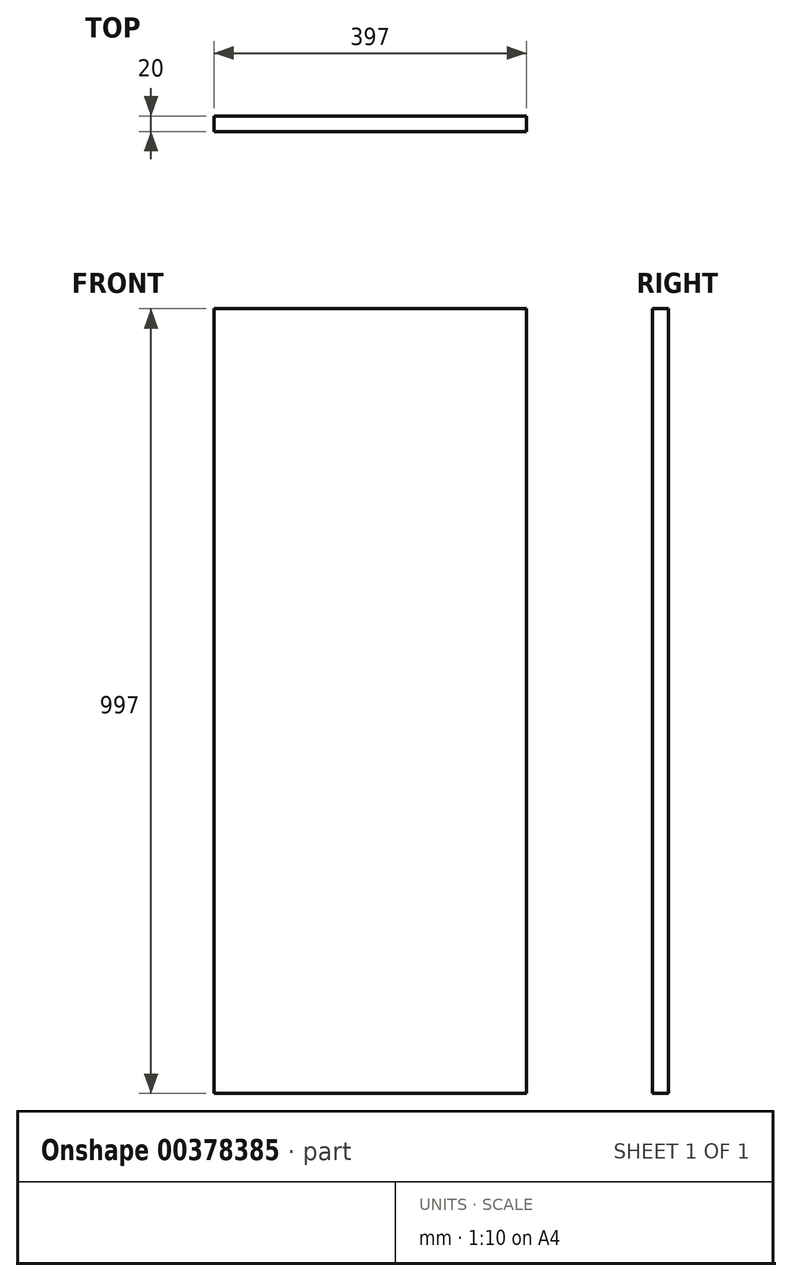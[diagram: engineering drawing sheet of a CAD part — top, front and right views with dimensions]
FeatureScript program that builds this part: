
annotation { "Feature Type Name" : "Feature", "Feature Type Description" : "" }
export const myFeature = defineFeature(function(context is Context, id is Id, definition is map)
    precondition{}
    {
        {
            var Q0;
            Q0=qCreatedBy(makeId("Front.planeOp"),FACE);
            var sketch = newSketch(context, id + "F0", { "sketchPlane" : qUnion([Q0])});
            skLineSegment(sketch, "E0.bottom", {"start": v(198.5, 498.5) * mm, "end": v(-198.5, 498.5) * mm});
            skLineSegment(sketch, "E0.top", {"start": v(198.5, -498.5) * mm, "end": v(-198.5, -498.5) * mm});
            skLineSegment(sketch, "E0.left", {"start": v(198.5, 498.5) * mm, "end": v(198.5, -498.5) * mm});
            skLineSegment(sketch, "E0.right", {"start": v(-198.5, 498.5) * mm, "end": v(-198.5, -498.5) * mm});
            skPoint(sketch, "E0.middle", {"position": v(0, 0) * mm});
            skSolve(sketch);
        }
        {
            var Q0;
            Q0=qSketchRegion(id+"F0",true);
            extrude(context, id + "F1", {"entities" : qUnion([Q0]), "depth" : 20 * mm});
        }
    });
